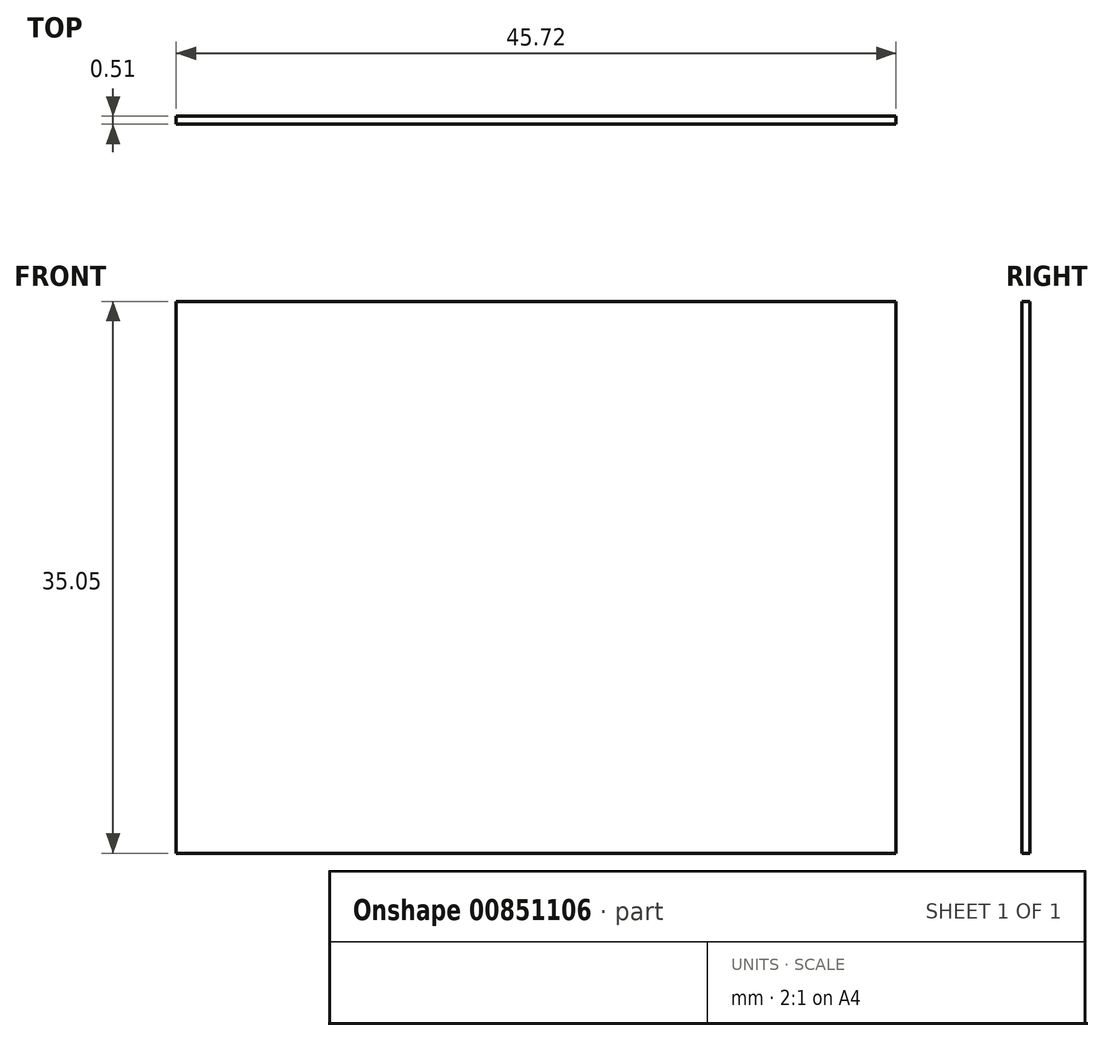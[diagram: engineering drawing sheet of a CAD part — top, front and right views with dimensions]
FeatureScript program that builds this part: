
annotation { "Feature Type Name" : "Feature", "Feature Type Description" : "" }
export const myFeature = defineFeature(function(context is Context, id is Id, definition is map)
    precondition{}
    {
        {
            var Q0;
            Q0=qCreatedBy(makeId("Front.planeOp"),FACE);
            var sketch = newSketch(context, id + "F0", { "sketchPlane" : qUnion([Q0])});
            skLineSegment(sketch, "E0", {"start": v(-63.15, 0) * mm, "end": v(-17.43, 0) * mm});
            skLineSegment(sketch, "E1", {"start": v(-63.15, 0) * mm, "end": v(-63.15, -35.05) * mm});
            skLineSegment(sketch, "E2", {"start": v(-17.43, 0) * mm, "end": v(-17.43, -35.05) * mm});
            skPoint(sketch, "E3", {"position": v(-40.3, 0) * mm});
            skLineSegment(sketch, "E4", {"start": v(-17.43, -35.05) * mm, "end": v(-63.15, -35.05) * mm});
            skSolve(sketch);
        }
        {
            var Q0;
            Q0=sQuery(id+"F0.wireOp",EDGE,"E1");
            var Q1;
            Q1=sQuery(id+"F0.wireOp",EDGE,"E2");
            var Q2;
            Q2=sQuery(id+"F0.wireOp",EDGE,"E0");
            extrude(context, id + "F1", {"bodyType" : ToolBodyType.SURFACE, "surfaceEntities" : qUnion([Q0, Q1, Q2]), "depth" : 7.62 * mm, "offsetDistance" : 25.4 * mm});
        }
        {
            var Q0;
            Q0=makeQuery(id+"F0.imprint","IMPRINT",FACE,{"disambiguationData":[TD([[makeQuery(id+"F0.imprint","IMPRINT",EDGE,{"derivedFrom":sQuery(id+"F0.wireOp",EDGE,"E0")}),-1.0]])]});
            extrude(context, id + "F2", {"entities" : qUnion([Q0]), "surfaceOperationType" : NewSurfaceOperationType.ADD, "oppositeDirection" : true, "depth" : 0.5 * mm, "offsetDistance" : 25.4 * mm});
        }
    });
